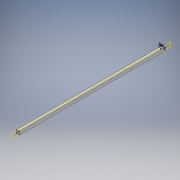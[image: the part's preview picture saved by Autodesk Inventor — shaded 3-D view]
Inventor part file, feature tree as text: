
AUTODESK INVENTOR PART (.ipt)
format: ipt  version: 2019 (Build 230136000, 136)  size: 135,680 bytes
history: native  units: in
note: dims shown in document units (in); Inventor stores cm internally (conversion verified against a paired STEP export)
features: extrude x2, sketch x2, other x2, pattern_linear x1, plane x1
ambient origin geometry x8: Origin, YZ Plane, XZ Plane, XY Plane, X Axis, Y Axis, Z Axis, Center Point
bodies: Solid1 (feature_tree)
feature tree (8):
  extrude  "Extrusion1"  Depth=1.9685in
  extrude  "Extrusion2"  Depth=0.1969in
  pattern_linear  "Rectangular Pattern1"  Count1=200 Spacing1=0.0in
  plane  "Work Plane1"
  sketch  "Sketch1"  dims[d0=1.9685in d1=1.9685in]
  sketch  "Sketch2"  dims[d2=0.315in d3=0.1969in d4=78.7402in d5=0.0in d6=0.7874in d7=3.937in d8=1.5748in d10=17.7165in d11=0.3937in d13=0.3937in d22=0.2362in d23=236.2205in d24=0.0in d25=0.7874in d27=17.7165in]
  other  "Work Axis1"
  other  "Work Axis2"
